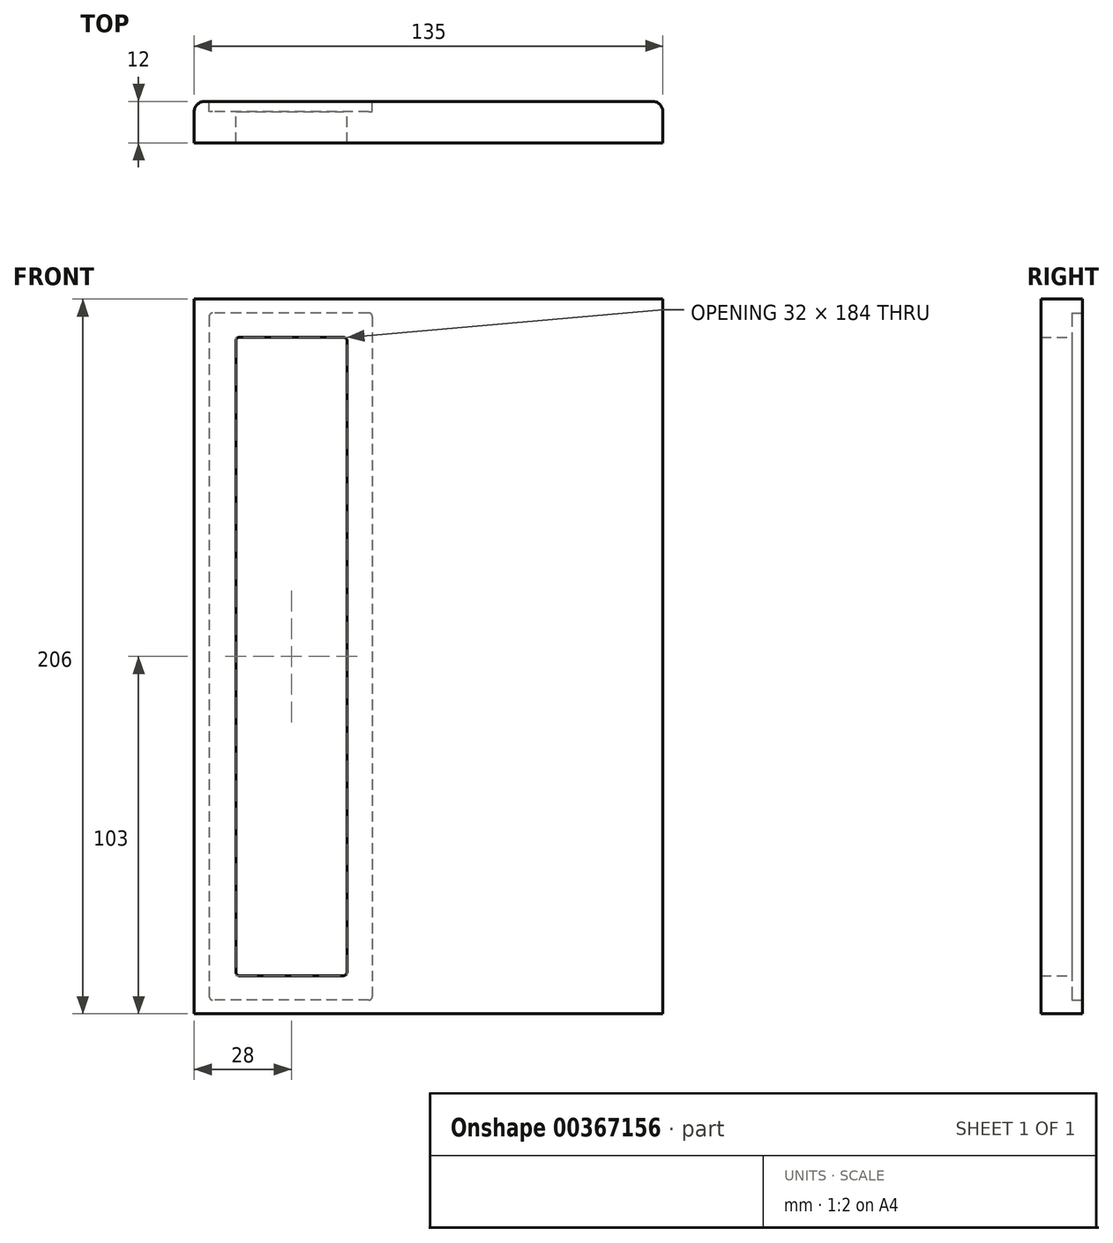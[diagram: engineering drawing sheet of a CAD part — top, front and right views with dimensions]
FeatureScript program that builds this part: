
annotation { "Feature Type Name" : "Feature", "Feature Type Description" : "" }
export const myFeature = defineFeature(function(context is Context, id is Id, definition is map)
    precondition{}
    {
        {
            var Q0;
            Q0=qCreatedBy(makeId("Front.planeOp"),FACE);
            var sketch = newSketch(context, id + "F0", { "sketchPlane" : qUnion([Q0])});
            skLineSegment(sketch, "E0.bottom", {"start": v(67.5, 103) * mm, "end": v(-67.5, 103) * mm});
            skLineSegment(sketch, "E0.top", {"start": v(67.5, -103) * mm, "end": v(-67.5, -103) * mm});
            skLineSegment(sketch, "E0.left", {"start": v(67.5, 103) * mm, "end": v(67.5, -103) * mm});
            skLineSegment(sketch, "E0.right", {"start": v(-67.5, 103) * mm, "end": v(-67.5, -103) * mm});
            skLineSegment(sketch, "E1.bottom", {"start": v(-16.2, 98) * mm, "end": v(-16.2, -98) * mm});
            skLineSegment(sketch, "E1.top", {"start": v(-63.2, 98) * mm, "end": v(-63.2, -98) * mm});
            skLineSegment(sketch, "E1.left", {"start": v(-17.2, 99) * mm, "end": v(-62.2, 99) * mm});
            skLineSegment(sketch, "E1.right", {"start": v(-17.2, -99) * mm, "end": v(-62.2, -99) * mm});
            skLineSegment(sketch, "E2.bottom", {"start": v(-53, 93.5) * mm, "end": v(-54.2, 93.5) * mm, "construction": true});
            skLineSegment(sketch, "E2.top", {"start": v(-53, -93.5) * mm, "end": v(-54.2, -93.5) * mm, "construction": true});
            skLineSegment(sketch, "E2.left", {"start": v(-53, 93.5) * mm, "end": v(-53, -93.5) * mm, "construction": true});
            skLineSegment(sketch, "E2.right", {"start": v(-54.2, 93.5) * mm, "end": v(-54.2, -93.5) * mm, "construction": true});
            skLineSegment(sketch, "E3.bottom", {"start": v(-54.5, 92) * mm, "end": v(-24.5, 92) * mm});
            skLineSegment(sketch, "E3.top", {"start": v(-54.5, -92) * mm, "end": v(-24.5, -92) * mm});
            skLineSegment(sketch, "E3.left", {"start": v(-55.5, 91) * mm, "end": v(-55.5, -91) * mm});
            skLineSegment(sketch, "E3.right", {"start": v(-23.5, 91) * mm, "end": v(-23.5, -91) * mm});
            skPoint(sketch, "E4.visualSharp", {"position": v(-16.2, 99) * mm});
            skArc(sketch, "E4.filletArc", {"start": v(-16.2, 98) * mm, "mid": v(-16.5, 98.7) * mm, "end": v(-17.2, 99) * mm});
            skPoint(sketch, "E5.visualSharp", {"position": v(-63.2, 99) * mm});
            skArc(sketch, "E5.filletArc", {"start": v(-62.2, 99) * mm, "mid": v(-62.9, 98.7) * mm, "end": v(-63.2, 98) * mm});
            skPoint(sketch, "E6.visualSharp", {"position": v(-63.2, -99) * mm});
            skArc(sketch, "E6.filletArc", {"start": v(-63.2, -98) * mm, "mid": v(-62.9, -98.7) * mm, "end": v(-62.2, -99) * mm});
            skPoint(sketch, "E7.visualSharp", {"position": v(-16.2, -99) * mm});
            skArc(sketch, "E7.filletArc", {"start": v(-17.2, -99) * mm, "mid": v(-16.5, -98.7) * mm, "end": v(-16.2, -98) * mm});
            skPoint(sketch, "E8.visualSharp", {"position": v(-23.5, -92) * mm});
            skArc(sketch, "E8.filletArc", {"start": v(-24.5, -92) * mm, "mid": v(-23.8, -91.7) * mm, "end": v(-23.5, -91) * mm});
            skPoint(sketch, "E9.visualSharp", {"position": v(-55.5, -92) * mm});
            skArc(sketch, "E9.filletArc", {"start": v(-55.5, -91) * mm, "mid": v(-55.2, -91.7) * mm, "end": v(-54.5, -92) * mm});
            skPoint(sketch, "E10.visualSharp", {"position": v(-55.5, 92) * mm});
            skArc(sketch, "E10.filletArc", {"start": v(-54.5, 92) * mm, "mid": v(-55.2, 91.7) * mm, "end": v(-55.5, 91) * mm});
            skPoint(sketch, "E11.visualSharp", {"position": v(-23.5, 92) * mm});
            skArc(sketch, "E11.filletArc", {"start": v(-23.5, 91) * mm, "mid": v(-23.8, 91.7) * mm, "end": v(-24.5, 92) * mm});
            skSolve(sketch);
        }
        {
            var Q0;
            Q0=makeQuery(id+"F0.imprint","IMPRINT",FACE,{"disambiguationData":[TD([[makeQuery(id+"F0.imprint","IMPRINT",EDGE,{"derivedFrom":sQuery(id+"F0.wireOp",EDGE,"E0.bottom")}),1.0]])]});
            var Q1;
            Q1=makeQuery(id+"F0.imprint","IMPRINT",FACE,{"disambiguationData":[TD([[makeQuery(id+"F0.imprint","IMPRINT",EDGE,{"derivedFrom":sQuery(id+"F0.wireOp",EDGE,"E1.bottom")}),-1.0]])]});
            extrude(context, id + "F1", {"entities" : qUnion([Q0, Q1]), "depth" : 12 * mm});
        }
        {
            var Q0;
            Q0=makeQuery(id+"F0.imprint","IMPRINT",FACE,{"disambiguationData":[TD([[makeQuery(id+"F0.imprint","IMPRINT",EDGE,{"derivedFrom":sQuery(id+"F0.wireOp",EDGE,"E1.bottom")}),-1.0]])]});
            extrude(context, id + "F2", {"entities" : qUnion([Q0]), "operationType" : NewBodyOperationType.REMOVE, "depth" : 3 * mm});
        }
        {
            var Q0;
            Q0=makeQuery(id+"F1.opExtrude","CAP_EDGE",EDGE,{"disambiguationData":[OSD([sQuery(id+"F0.wireOp",EDGE,"E0.left")])],"isStart":true});
            var Q1;
            Q1=makeQuery(id+"F1.opExtrude","CAP_EDGE",EDGE,{"disambiguationData":[OSD([sQuery(id+"F0.wireOp",EDGE,"E0.right")])],"isStart":true});
            fillet(context, id + "F3", {"entities" : qUnion([Q0, Q1]), "radius" : 3 * mm, "tangentPropagation" : true, "allowEdgeOverflow" : false});
        }
    });
